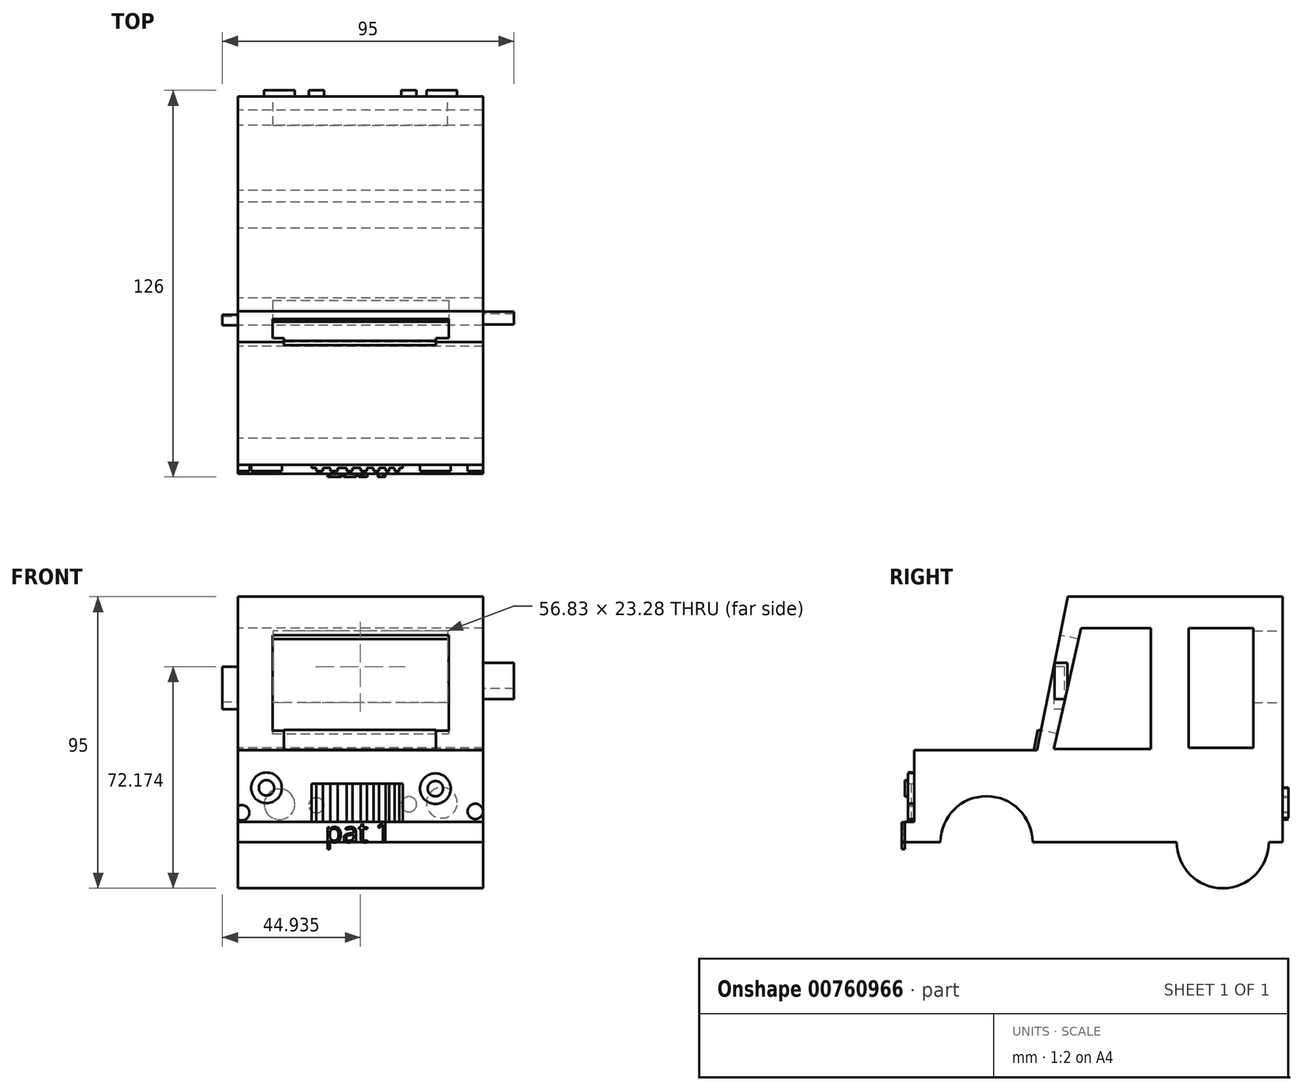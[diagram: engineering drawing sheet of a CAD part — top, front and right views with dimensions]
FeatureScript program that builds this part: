
annotation { "Feature Type Name" : "Feature", "Feature Type Description" : "" }
export const myFeature = defineFeature(function(context is Context, id is Id, definition is map)
    precondition{}
    {
        {
            var Q0;
            Q0=qCreatedBy(makeId("Right.planeOp"),FACE);
            var sketch = newSketch(context, id + "F0", { "sketchPlane" : qUnion([Q0])});
            skLineSegment(sketch, "E0", {"start": v(-60.4, -27.4) * mm, "end": v(59.6, -27.4) * mm});
            skLineSegment(sketch, "E1", {"start": v(59.6, -27.4) * mm, "end": v(59.6, 52.6) * mm});
            skLineSegment(sketch, "E2", {"start": v(59.6, 52.6) * mm, "end": v(-10.4, 52.6) * mm});
            skLineSegment(sketch, "E3", {"start": v(-10.4, 52.6) * mm, "end": v(-20.4, 2.6) * mm});
            skLineSegment(sketch, "E4", {"start": v(-20.4, 2.6) * mm, "end": v(-60.4, 2.6) * mm});
            skLineSegment(sketch, "E5", {"start": v(-60.4, 2.6) * mm, "end": v(-60.4, -27.4) * mm});
            skCircle(sketch, "E6", {"center": v(-36.83, -27.4) * mm, "radius": 15 * mm});
            skCircle(sketch, "E7", {"center": v(40.14, -27.4) * mm, "radius": 15 * mm});
            skSolve(sketch);
        }
        {
            var Q0;
            {var subQ0=sQuery(id+"F0.wireOp",EDGE,"E1");Q0=makeQuery(id+"F0.imprint","IMPRINT",FACE,{"disambiguationData":[TD([[makeQuery(id+"F0.imprint","IMPRINT",EDGE,{"derivedFrom":subQ0}),1.0]])]});}
            var Q1;
            {var subQ0=sQuery(id+"F0.wireOp",EDGE,"E6");var subQ1=sQuery(id+"F0.wireOp",EDGE,"E0");var subQ2=makeQuery(id+"F0.imprint","INTERSECT",VERTEX,{"disambiguationData":[OD(0.0)],"derivedFrom":[subQ1,subQ0]});Q1=makeQuery(id+"F0.imprint","IMPRINT",FACE,{"disambiguationData":[TD([[makeQuery(id+"F0.imprint","IMPRINT",EDGE,{"disambiguationData":[TD([[subQ2,-1.0]])],"derivedFrom":subQ1}),-1.0]])]});}
            var Q2;
            {var subQ0=sQuery(id+"F0.wireOp",EDGE,"E6");var subQ1=sQuery(id+"F0.wireOp",EDGE,"E0");var subQ2=makeQuery(id+"F0.imprint","INTERSECT",VERTEX,{"disambiguationData":[OD(0.0)],"derivedFrom":[subQ1,subQ0]});Q2=makeQuery(id+"F0.imprint","IMPRINT",FACE,{"disambiguationData":[TD([[makeQuery(id+"F0.imprint","IMPRINT",EDGE,{"disambiguationData":[TD([[subQ2,-1.0]])],"derivedFrom":subQ1}),1.0]])]});}
            var Q3;
            {var subQ0=sQuery(id+"F0.wireOp",EDGE,"E7");var subQ1=sQuery(id+"F0.wireOp",EDGE,"E0");var subQ2=makeQuery(id+"F0.imprint","INTERSECT",VERTEX,{"disambiguationData":[OD(0.0)],"derivedFrom":[subQ1,subQ0]});Q3=makeQuery(id+"F0.imprint","IMPRINT",FACE,{"disambiguationData":[TD([[makeQuery(id+"F0.imprint","IMPRINT",EDGE,{"disambiguationData":[TD([[subQ2,-1.0]])],"derivedFrom":subQ1}),-1.0]])]});}
            var Q4;
            {var subQ0=sQuery(id+"F0.wireOp",EDGE,"E7");var subQ1=sQuery(id+"F0.wireOp",EDGE,"E0");var subQ2=makeQuery(id+"F0.imprint","INTERSECT",VERTEX,{"disambiguationData":[OD(0.0)],"derivedFrom":[subQ1,subQ0]});Q4=makeQuery(id+"F0.imprint","IMPRINT",FACE,{"disambiguationData":[TD([[makeQuery(id+"F0.imprint","IMPRINT",EDGE,{"disambiguationData":[TD([[subQ2,-1.0]])],"derivedFrom":subQ1}),1.0]])]});}
            extrude(context, id + "F1", {"entities" : qUnion([Q0, Q1, Q2, Q3, Q4]), "depth" : 80 * mm, "offsetDistance" : 25 * mm});
        }
        {
            var Q0;
            Q0=makeQuery(id+"F1.opExtrude","SWEPT_FACE",FACE,{"disambiguationData":[OSD([sQuery(id+"F0.wireOp",EDGE,"E5")])]});
            var sketch = newSketch(context, id + "F2", { "sketchPlane" : qUnion([Q0])});
            skCircle(sketch, "E8", {"center": v(9.38, -9.68) * mm, "radius": 5 * mm});
            skCircle(sketch, "E9", {"center": v(64.4, -9.94) * mm, "radius": 5 * mm});
            skSolve(sketch);
        }
        {
            var Q0;
            Q0=makeQuery(id+"F2.imprint","IMPRINT",FACE,{"disambiguationData":[TD([[makeQuery(id+"F2.imprint","IMPRINT",EDGE,{"derivedFrom":sQuery(id+"F2.wireOp",EDGE,"E8")}),1.0]])]});
            var Q1;
            Q1=makeQuery(id+"F2.imprint","IMPRINT",FACE,{"disambiguationData":[TD([[makeQuery(id+"F2.imprint","IMPRINT",EDGE,{"derivedFrom":sQuery(id+"F2.wireOp",EDGE,"E9")}),1.0]])]});
            extrude(context, id + "F3", {"entities" : qUnion([Q0, Q1]), "operationType" : NewBodyOperationType.ADD, "depth" : 2 * mm, "offsetDistance" : 25 * mm});
        }
        {
            var Q0;
            Q0=makeQuery(id+"F1.opExtrude","SWEPT_FACE",FACE,{"disambiguationData":[OSD([sQuery(id+"F0.wireOp",EDGE,"E3")])]});
            var sketch = newSketch(context, id + "F4", { "sketchPlane" : qUnion([Q0])});
            skLineSegment(sketch, "E10.bottom", {"start": v(11.33, 36.75) * mm, "end": v(68.74, 36.75) * mm});
            skLineSegment(sketch, "E10.top", {"start": v(11.33, 5.1) * mm, "end": v(68.74, 5.1) * mm});
            skLineSegment(sketch, "E10.left", {"start": v(11.33, 36.75) * mm, "end": v(11.33, 5.1) * mm});
            skLineSegment(sketch, "E10.right", {"start": v(68.74, 36.75) * mm, "end": v(68.74, 5.1) * mm});
            skSolve(sketch);
        }
        {
            var Q0;
            Q0=makeQuery(id+"F4.imprint","IMPRINT",FACE,{"disambiguationData":[TD([[makeQuery(id+"F4.imprint","IMPRINT",EDGE,{"derivedFrom":sQuery(id+"F4.wireOp",EDGE,"E10.bottom")}),-1.0]])]});
            extrude(context, id + "F5", {"entities" : qUnion([Q0]), "operationType" : NewBodyOperationType.REMOVE, "oppositeDirection" : true, "depth" : 25 * mm, "offsetDistance" : 25 * mm});
        }
        {
            var Q0;
            Q0=makeQuery(id+"F1.opExtrude","SWEPT_FACE",FACE,{"disambiguationData":[OSD([sQuery(id+"F0.wireOp",EDGE,"E1")])]});
            var sketch = newSketch(context, id + "F6", { "sketchPlane" : qUnion([Q0])});
            skLineSegment(sketch, "E11.bottom", {"start": v(-68.35, 41.41) * mm, "end": v(-11.52, 41.41) * mm});
            skLineSegment(sketch, "E11.top", {"start": v(-68.35, 18.14) * mm, "end": v(-11.52, 18.14) * mm});
            skLineSegment(sketch, "E11.left", {"start": v(-68.35, 41.41) * mm, "end": v(-68.35, 18.14) * mm});
            skLineSegment(sketch, "E11.right", {"start": v(-11.52, 41.41) * mm, "end": v(-11.52, 18.14) * mm});
            skSolve(sketch);
        }
        {
            var Q0;
            Q0=makeQuery(id+"F6.imprint","IMPRINT",FACE,{"disambiguationData":[TD([[makeQuery(id+"F6.imprint","IMPRINT",EDGE,{"derivedFrom":sQuery(id+"F6.wireOp",EDGE,"E11.bottom")}),1.0]])]});
            var sketch = newSketch(context, id + "F7", { "sketchPlane" : qUnion([Q0])});
            skCircle(sketch, "E12", {"center": v(-66.49, -14.54) * mm, "radius": 5 * mm});
            skCircle(sketch, "E13", {"center": v(-13.63, -15.03) * mm, "radius": 5 * mm});
            skCircle(sketch, "E14", {"center": v(-55.79, -15.03) * mm, "radius": 2.5 * mm});
            skCircle(sketch, "E15", {"center": v(-25.65, -15.36) * mm, "radius": 2.5 * mm});
            skSolve(sketch);
        }
        {
            var Q0;
            Q0=makeQuery(id+"F6.imprint","IMPRINT",FACE,{"disambiguationData":[TD([[makeQuery(id+"F6.imprint","IMPRINT",EDGE,{"derivedFrom":sQuery(id+"F6.wireOp",EDGE,"E11.bottom")}),-1.0]])]});
            extrude(context, id + "F8", {"entities" : qUnion([Q0]), "operationType" : NewBodyOperationType.REMOVE, "oppositeDirection" : true, "depth" : 25 * mm, "offsetDistance" : 25 * mm});
        }
        {
            var Q0;
            Q0=makeQuery(id+"F7.imprint","IMPRINT",FACE,{"disambiguationData":[TD([[makeQuery(id+"F7.imprint","IMPRINT",EDGE,{"derivedFrom":sQuery(id+"F7.wireOp",EDGE,"E12")}),1.0]])]});
            var Q1;
            Q1=makeQuery(id+"F7.imprint","IMPRINT",FACE,{"disambiguationData":[TD([[makeQuery(id+"F7.imprint","IMPRINT",EDGE,{"derivedFrom":sQuery(id+"F7.wireOp",EDGE,"E14")}),1.0]])]});
            var Q2;
            Q2=makeQuery(id+"F7.imprint","IMPRINT",FACE,{"disambiguationData":[TD([[makeQuery(id+"F7.imprint","IMPRINT",EDGE,{"derivedFrom":sQuery(id+"F7.wireOp",EDGE,"E13")}),1.0]])]});
            var Q3;
            Q3=makeQuery(id+"F7.imprint","IMPRINT",FACE,{"disambiguationData":[TD([[makeQuery(id+"F7.imprint","IMPRINT",EDGE,{"derivedFrom":sQuery(id+"F7.wireOp",EDGE,"E15")}),1.0]])]});
            extrude(context, id + "F9", {"entities" : qUnion([Q0, Q1, Q2, Q3]), "operationType" : NewBodyOperationType.ADD, "depth" : 2 * mm, "offsetDistance" : 25 * mm});
        }
        {
            var Q0;
            Q0=makeQuery(id+"F1.opExtrude","CAP_FACE",FACE,{"disambiguationData":[OSD([sQuery(id+"F0.wireOp",EDGE,"E0"),sQuery(id+"F0.wireOp",EDGE,"E1"),sQuery(id+"F0.wireOp",EDGE,"E2"),sQuery(id+"F0.wireOp",EDGE,"E3"),sQuery(id+"F0.wireOp",EDGE,"E4"),sQuery(id+"F0.wireOp",EDGE,"E5"),sQuery(id+"F0.wireOp",EDGE,"E6"),sQuery(id+"F0.wireOp",EDGE,"E7")])],"isStart":true});
            var sketch = newSketch(context, id + "F10", { "sketchPlane" : qUnion([Q0])});
            skLineSegment(sketch, "E16", {"start": v(-16.68, 42.4) * mm, "end": v(6.01, 42.4) * mm});
            skLineSegment(sketch, "E17", {"start": v(6.01, 42.4) * mm, "end": v(14.94, 2.99) * mm});
            skLineSegment(sketch, "E18", {"start": v(14.94, 2.99) * mm, "end": v(-16.68, 2.99) * mm});
            skLineSegment(sketch, "E19", {"start": v(-16.68, 2.99) * mm, "end": v(-16.68, 42.4) * mm});
            skSolve(sketch);
        }
        {
            var Q0;
            Q0=makeQuery(id+"F10.imprint","IMPRINT",FACE,{"disambiguationData":[TD([[makeQuery(id+"F10.imprint","IMPRINT",EDGE,{"derivedFrom":sQuery(id+"F10.wireOp",EDGE,"E16")}),1.0]])]});
            var sketch = newSketch(context, id + "F11", { "sketchPlane" : qUnion([Q0])});
            skLineSegment(sketch, "E20.bottom", {"start": v(-50.14, 42.38) * mm, "end": v(-29, 42.38) * mm});
            skLineSegment(sketch, "E20.top", {"start": v(-50.14, 3.4) * mm, "end": v(-29, 3.4) * mm});
            skLineSegment(sketch, "E20.left", {"start": v(-50.14, 42.38) * mm, "end": v(-50.14, 3.4) * mm});
            skLineSegment(sketch, "E20.right", {"start": v(-29, 42.38) * mm, "end": v(-29, 3.4) * mm});
            skSolve(sketch);
        }
        {
            var Q0;
            Q0=makeQuery(id+"F11.imprint","IMPRINT",FACE,{"disambiguationData":[TD([[makeQuery(id+"F11.imprint","IMPRINT",EDGE,{"derivedFrom":sQuery(id+"F11.wireOp",EDGE,"E20.bottom")}),-1.0]])]});
            var Q1;
            Q1=makeQuery(id+"F11.imprint","IMPRINT",FACE,{"disambiguationData":[TD([[makeQuery(id+"F11.imprint","IMPRINT",EDGE,{"derivedFrom":makeQuery(id+"F10.imprint","IMPRINT",EDGE,{"derivedFrom":sQuery(id+"F10.wireOp",EDGE,"E16")})}),-1.0]])]});
            extrude(context, id + "F12", {"entities" : qUnion([Q0, Q1]), "operationType" : NewBodyOperationType.REMOVE, "oppositeDirection" : true, "depth" : 100 * mm, "offsetDistance" : 25 * mm});
        }
        {
            var Q0;
            Q0=makeQuery(id+"F1.opExtrude","SWEPT_FACE",FACE,{"disambiguationData":[OSD([sQuery(id+"F0.wireOp",EDGE,"E3")])]});
            var sketch = newSketch(context, id + "F13", { "sketchPlane" : qUnion([Q0])});
            skLineSegment(sketch, "E21.bottom", {"start": v(15, 5.1) * mm, "end": v(64.59, 5.1) * mm});
            skLineSegment(sketch, "E21.top", {"start": v(15, -1.45) * mm, "end": v(64.59, -1.45) * mm});
            skLineSegment(sketch, "E21.left", {"start": v(15, 5.1) * mm, "end": v(15, -1.45) * mm});
            skLineSegment(sketch, "E21.right", {"start": v(64.59, 5.1) * mm, "end": v(64.59, -1.45) * mm});
            skSolve(sketch);
        }
        {
            var Q0;
            Q0=makeQuery(id+"F13.imprint","IMPRINT",FACE,{"disambiguationData":[TD([[makeQuery(id+"F13.imprint","IMPRINT",EDGE,{"derivedFrom":sQuery(id+"F13.wireOp",EDGE,"E21.bottom")}),-1.0]])]});
            extrude(context, id + "F14", {"entities" : qUnion([Q0]), "operationType" : NewBodyOperationType.ADD, "depth" : 1 * mm, "offsetDistance" : 25 * mm});
        }
        {
            var Q0;
            Q0=makeQuery(id+"F1.opExtrude","SWEPT_FACE",FACE,{"disambiguationData":[OSD([sQuery(id+"F0.wireOp",EDGE,"E5")])]});
            var sketch = newSketch(context, id + "F15", { "sketchPlane" : qUnion([Q0])});
            skLineSegment(sketch, "E22.bottom", {"start": v(0, -20.79) * mm, "end": v(80, -20.79) * mm});
            skLineSegment(sketch, "E22.top", {"start": v(0, -27.4) * mm, "end": v(80, -27.4) * mm});
            skLineSegment(sketch, "E22.left", {"start": v(0, -20.79) * mm, "end": v(0, -27.4) * mm});
            skLineSegment(sketch, "E22.right", {"start": v(80, -20.79) * mm, "end": v(80, -27.4) * mm});
            skSolve(sketch);
        }
        {
            var Q0;
            Q0=makeQuery(id+"F15.imprint","IMPRINT",FACE,{"disambiguationData":[TD([[makeQuery(id+"F15.imprint","IMPRINT",EDGE,{"derivedFrom":sQuery(id+"F15.wireOp",EDGE,"E22.bottom")}),-1.0]])]});
            extrude(context, id + "F16", {"entities" : qUnion([Q0]), "operationType" : NewBodyOperationType.ADD, "depth" : 3 * mm, "offsetDistance" : 25 * mm});
        }
        {
            var Q0;
            Q0=makeQuery(id+"F1.opExtrude","SWEPT_FACE",FACE,{"disambiguationData":[OSD([sQuery(id+"F0.wireOp",EDGE,"E5")])]});
            var sketch = newSketch(context, id + "F17", { "sketchPlane" : qUnion([Q0])});
            skCircle(sketch, "E23", {"center": v(1.31, -17.78) * mm, "radius": 2.5 * mm});
            skCircle(sketch, "E24", {"center": v(77.4, -17.35) * mm, "radius": 2.5 * mm});
            skSolve(sketch);
        }
        {
            var Q0;
            {var subQ0=sQuery(id+"F17.wireOp",EDGE,"E23");var subQ1=makeQuery(id+"F1.opExtrude","CAP_EDGE",EDGE,{"disambiguationData":[OSD([sQuery(id+"F0.wireOp",EDGE,"E5")])],"isStart":true});var subQ2=makeQuery(id+"F17.imprint","INTERSECT",VERTEX,{"disambiguationData":[OD(0.0)],"derivedFrom":[subQ1,subQ0]});Q0=makeQuery(id+"F17.imprint","IMPRINT",FACE,{"disambiguationData":[TD([[makeQuery(id+"F17.imprint","IMPRINT",EDGE,{"disambiguationData":[TD([[subQ2,1.0]])],"derivedFrom":subQ0}),1.0]])]});}
            var Q1;
            Q1=makeQuery(id+"F17.imprint","IMPRINT",FACE,{"disambiguationData":[TD([[makeQuery(id+"F17.imprint","IMPRINT",EDGE,{"derivedFrom":sQuery(id+"F17.wireOp",EDGE,"E24")}),1.0]])]});
            extrude(context, id + "F18", {"entities" : qUnion([Q0, Q1]), "operationType" : NewBodyOperationType.ADD, "depth" : 2 * mm, "offsetDistance" : 25 * mm});
        }
        {
            var Q0;
            Q0=makeQuery(id+"F1.opExtrude","SWEPT_FACE",FACE,{"disambiguationData":[OSD([sQuery(id+"F0.wireOp",EDGE,"E5")])]});
            var sketch = newSketch(context, id + "F19", { "sketchPlane" : qUnion([Q0])});
            skLineSegment(sketch, "E25.bottom", {"start": v(24.1, -8.3) * mm, "end": v(53.73, -8.3) * mm});
            skLineSegment(sketch, "E25.top", {"start": v(24.1, -20.79) * mm, "end": v(53.73, -20.79) * mm});
            skLineSegment(sketch, "E25.left", {"start": v(24.1, -8.3) * mm, "end": v(24.1, -20.79) * mm});
            skLineSegment(sketch, "E25.right", {"start": v(53.73, -8.3) * mm, "end": v(53.73, -20.79) * mm});
            skSolve(sketch);
        }
        {
            var Q0;
            Q0=makeQuery(id+"F19.imprint","IMPRINT",FACE,{"disambiguationData":[TD([[makeQuery(id+"F19.imprint","IMPRINT",EDGE,{"derivedFrom":sQuery(id+"F19.wireOp",EDGE,"E25.bottom")}),-1.0]])]});
            extrude(context, id + "F20", {"entities" : qUnion([Q0]), "operationType" : NewBodyOperationType.ADD, "depth" : 1 * mm, "offsetDistance" : 25 * mm});
        }
        {
            var Q0;
            Q0=makeQuery(id+"F20.opExtrude","CAP_FACE",FACE,{"disambiguationData":[OSD([sQuery(id+"F19.wireOp",EDGE,"E25.bottom"),sQuery(id+"F19.wireOp",EDGE,"E25.top"),sQuery(id+"F19.wireOp",EDGE,"E25.left"),sQuery(id+"F19.wireOp",EDGE,"E25.right")])],"isStart":false});
            var sketch = newSketch(context, id + "F21", { "sketchPlane" : qUnion([Q0])});
            skLineSegment(sketch, "E26.bottom", {"start": v(25.56, -8.3) * mm, "end": v(27.7, -8.3) * mm});
            skLineSegment(sketch, "E26.top", {"start": v(25.56, -20.79) * mm, "end": v(27.7, -20.79) * mm});
            skLineSegment(sketch, "E26.left", {"start": v(25.56, -8.3) * mm, "end": v(25.56, -20.79) * mm});
            skLineSegment(sketch, "E26.right", {"start": v(27.7, -8.3) * mm, "end": v(27.7, -20.79) * mm});
            skLineSegment(sketch, "E27.bottom", {"start": v(30.22, -8.3) * mm, "end": v(32.55, -8.3) * mm});
            skLineSegment(sketch, "E27.top", {"start": v(30.22, -20.79) * mm, "end": v(32.55, -20.79) * mm});
            skLineSegment(sketch, "E27.left", {"start": v(30.22, -8.3) * mm, "end": v(30.22, -20.79) * mm});
            skLineSegment(sketch, "E27.right", {"start": v(32.55, -8.3) * mm, "end": v(32.55, -20.79) * mm});
            skLineSegment(sketch, "E28.bottom", {"start": v(35.46, -8.3) * mm, "end": v(37.4, -8.3) * mm});
            skLineSegment(sketch, "E28.top", {"start": v(35.46, -20.79) * mm, "end": v(37.4, -20.79) * mm});
            skLineSegment(sketch, "E28.left", {"start": v(35.46, -8.3) * mm, "end": v(35.46, -20.79) * mm});
            skLineSegment(sketch, "E28.right", {"start": v(37.4, -8.3) * mm, "end": v(37.4, -20.79) * mm});
            skLineSegment(sketch, "E29.bottom", {"start": v(40.01, -8.3) * mm, "end": v(42.15, -8.3) * mm});
            skLineSegment(sketch, "E29.top", {"start": v(40.01, -20.79) * mm, "end": v(42.15, -20.79) * mm});
            skLineSegment(sketch, "E29.left", {"start": v(40.01, -8.3) * mm, "end": v(40.01, -20.79) * mm});
            skLineSegment(sketch, "E29.right", {"start": v(42.15, -8.3) * mm, "end": v(42.15, -20.79) * mm});
            skLineSegment(sketch, "E30.bottom", {"start": v(44.28, -8.3) * mm, "end": v(46.03, -8.3) * mm});
            skLineSegment(sketch, "E30.top", {"start": v(44.28, -20.79) * mm, "end": v(46.03, -20.79) * mm});
            skLineSegment(sketch, "E30.left", {"start": v(44.28, -8.3) * mm, "end": v(44.28, -20.79) * mm});
            skLineSegment(sketch, "E30.right", {"start": v(46.03, -8.3) * mm, "end": v(46.03, -20.79) * mm});
            skLineSegment(sketch, "E31.bottom", {"start": v(48.16, -8.3) * mm, "end": v(49.32, -8.3) * mm});
            skLineSegment(sketch, "E31.top", {"start": v(48.16, -20.79) * mm, "end": v(49.32, -20.79) * mm});
            skLineSegment(sketch, "E31.left", {"start": v(48.16, -8.3) * mm, "end": v(48.16, -20.79) * mm});
            skLineSegment(sketch, "E31.right", {"start": v(49.32, -8.3) * mm, "end": v(49.32, -20.79) * mm});
            skLineSegment(sketch, "E32.bottom", {"start": v(51.17, -8.3) * mm, "end": v(52.62, -8.3) * mm});
            skLineSegment(sketch, "E32.top", {"start": v(51.17, -20.79) * mm, "end": v(52.62, -20.79) * mm});
            skLineSegment(sketch, "E32.left", {"start": v(51.17, -8.3) * mm, "end": v(51.17, -20.79) * mm});
            skLineSegment(sketch, "E32.right", {"start": v(52.62, -8.3) * mm, "end": v(52.62, -20.79) * mm});
            skSolve(sketch);
        }
        {
            var Q0;
            Q0=makeQuery(id+"F21.imprint","IMPRINT",FACE,{"disambiguationData":[TD([[makeQuery(id+"F21.imprint","IMPRINT",EDGE,{"derivedFrom":sQuery(id+"F21.wireOp",EDGE,"E26.bottom")}),-1.0]])]});
            var Q1;
            Q1=makeQuery(id+"F21.imprint","IMPRINT",FACE,{"disambiguationData":[TD([[makeQuery(id+"F21.imprint","IMPRINT",EDGE,{"derivedFrom":sQuery(id+"F21.wireOp",EDGE,"E27.bottom")}),-1.0]])]});
            var Q2;
            Q2=makeQuery(id+"F21.imprint","IMPRINT",FACE,{"disambiguationData":[TD([[makeQuery(id+"F21.imprint","IMPRINT",EDGE,{"derivedFrom":sQuery(id+"F21.wireOp",EDGE,"E28.bottom")}),-1.0]])]});
            var Q3;
            Q3=makeQuery(id+"F21.imprint","IMPRINT",FACE,{"disambiguationData":[TD([[makeQuery(id+"F21.imprint","IMPRINT",EDGE,{"derivedFrom":sQuery(id+"F21.wireOp",EDGE,"E29.bottom")}),-1.0]])]});
            var Q4;
            Q4=makeQuery(id+"F21.imprint","IMPRINT",FACE,{"disambiguationData":[TD([[makeQuery(id+"F21.imprint","IMPRINT",EDGE,{"derivedFrom":sQuery(id+"F21.wireOp",EDGE,"E30.bottom")}),-1.0]])]});
            var Q5;
            Q5=makeQuery(id+"F21.imprint","IMPRINT",FACE,{"disambiguationData":[TD([[makeQuery(id+"F21.imprint","IMPRINT",EDGE,{"derivedFrom":sQuery(id+"F21.wireOp",EDGE,"E31.bottom")}),-1.0]])]});
            var Q6;
            Q6=makeQuery(id+"F21.imprint","IMPRINT",FACE,{"disambiguationData":[TD([[makeQuery(id+"F21.imprint","IMPRINT",EDGE,{"derivedFrom":sQuery(id+"F21.wireOp",EDGE,"E32.bottom")}),-1.0]])]});
            extrude(context, id + "F22", {"entities" : qUnion([Q0, Q1, Q2, Q3, Q4, Q5, Q6]), "operationType" : NewBodyOperationType.ADD, "depth" : 1 * mm, "offsetDistance" : 25 * mm});
        }
        {
            var Q0;
            Q0=makeQuery(id+"F16.opExtrude","CAP_FACE",FACE,{"disambiguationData":[OSD([sQuery(id+"F15.wireOp",EDGE,"E22.bottom"),sQuery(id+"F15.wireOp",EDGE,"E22.top"),sQuery(id+"F15.wireOp",EDGE,"E22.left"),sQuery(id+"F15.wireOp",EDGE,"E22.right")])],"isStart":false});
            var sketch = newSketch(context, id + "F23", { "sketchPlane" : qUnion([Q0])});
            skText(sketch, "E33", { "text": "pat 1", "fontName": "OpenSans-Regular.ttf"});
            const initialGuessF23  = {"E33": [0.0285, -0.0274, 1, 0, 0.00661]};
            skSetInitialGuess(sketch, initialGuessF23);
            skSolve(sketch);
        }
        {
            var Q0;
            Q0 = qSketchRegion(id + "F23", true);
            extrude(context, id + "F24", {"entities" : qUnion([Q0]), "operationType" : NewBodyOperationType.ADD, "depth" : 1 * mm, "offsetDistance" : 25 * mm});
        }
        {
            var Q0;
            Q0=makeQuery(id+"F3.opExtrude","CAP_FACE",FACE,{"disambiguationData":[OSD([sQuery(id+"F2.wireOp",EDGE,"E8")])],"isStart":false});
            var sketch = newSketch(context, id + "F25", { "sketchPlane" : qUnion([Q0])});
            skCircle(sketch, "E34", {"center": v(9.38, -9.68) * mm, "radius": 2.5 * mm});
            skSolve(sketch);
        }
        {
            var Q0;
            Q0=makeQuery(id+"F3.opExtrude","CAP_FACE",FACE,{"disambiguationData":[OSD([sQuery(id+"F2.wireOp",EDGE,"E9")])],"isStart":false});
            var sketch = newSketch(context, id + "F26", { "sketchPlane" : qUnion([Q0])});
            skCircle(sketch, "E35", {"center": v(64.4, -9.94) * mm, "radius": 2.5 * mm});
            skSolve(sketch);
        }
        {
            var Q0;
            Q0=makeQuery(id+"F26.imprint","IMPRINT",FACE,{"disambiguationData":[TD([[makeQuery(id+"F26.imprint","IMPRINT",EDGE,{"derivedFrom":sQuery(id+"F26.wireOp",EDGE,"E35")}),1.0]])]});
            var Q1;
            Q1=makeQuery(id+"F25.imprint","IMPRINT",FACE,{"disambiguationData":[TD([[makeQuery(id+"F25.imprint","IMPRINT",EDGE,{"derivedFrom":sQuery(id+"F25.wireOp",EDGE,"E34")}),1.0]])]});
            extrude(context, id + "F27", {"entities" : qUnion([Q0, Q1]), "operationType" : NewBodyOperationType.ADD, "depth" : 1 * mm, "offsetDistance" : 25 * mm});
        }
        {
            var Q0;
            Q0=makeQuery(id+"F10.imprint","IMPRINT",FACE,{"disambiguationData":[TD([[makeQuery(id+"F10.imprint","IMPRINT",EDGE,{"derivedFrom":sQuery(id+"F10.wireOp",EDGE,"E16")}),1.0]])]});
            var sketch = newSketch(context, id + "F28", { "sketchPlane" : qUnion([Q0])});
            skLineSegment(sketch, "E36.bottom", {"start": v(11.46, 29.77) * mm, "end": v(14.95, 29.77) * mm});
            skLineSegment(sketch, "E36.top", {"start": v(11.46, 16) * mm, "end": v(14.95, 16) * mm});
            skLineSegment(sketch, "E36.left", {"start": v(11.46, 29.77) * mm, "end": v(11.46, 16) * mm});
            skLineSegment(sketch, "E36.right", {"start": v(14.95, 29.77) * mm, "end": v(14.95, 16) * mm});
            skSolve(sketch);
        }
        {
            var Q0;
            {var subQ1=sQuery(id+"F28.wireOp",EDGE,"E36.bottom");Q0=makeQuery(id+"F28.imprint","IMPRINT",FACE,{"disambiguationData":[TD([[makeQuery(id+"F28.imprint","IMPRINT",EDGE,{"derivedFrom":subQ1}),-1.0]])]});}
            extrude(context, id + "F29", {"entities" : qUnion([Q0]), "operationType" : NewBodyOperationType.ADD, "depth" : 5 * mm, "offsetDistance" : 25 * mm});
        }
        {
            var Q0;
            Q0=makeQuery(id+"F16.boolean.opBoolean","MERGE",FACE,{"derivedFrom":[makeQuery(id+"F1.opExtrude","CAP_FACE",FACE,{"disambiguationData":[OSD([sQuery(id+"F0.wireOp",EDGE,"E0"),sQuery(id+"F0.wireOp",EDGE,"E1"),sQuery(id+"F0.wireOp",EDGE,"E2"),sQuery(id+"F0.wireOp",EDGE,"E3"),sQuery(id+"F0.wireOp",EDGE,"E4"),sQuery(id+"F0.wireOp",EDGE,"E5"),sQuery(id+"F0.wireOp",EDGE,"E6"),sQuery(id+"F0.wireOp",EDGE,"E7")])],"isStart":false}),makeQuery(id+"F16.opExtrude","SWEPT_FACE",FACE,{"disambiguationData":[OSD([sQuery(id+"F15.wireOp",EDGE,"E22.right")])]})]});
            var sketch = newSketch(context, id + "F30", { "sketchPlane" : qUnion([Q0])});
            skPoint(sketch, "E37.oppositeSnap0", {"position": v(-10.47, 22.7) * mm});
            skLineSegment(sketch, "E37.bottom", {"start": v(-14.7, 31.1) * mm, "end": v(-10.47, 31.1) * mm});
            skLineSegment(sketch, "E37.top", {"start": v(-14.7, 19.2) * mm, "end": v(-10.47, 19.2) * mm});
            skLineSegment(sketch, "E37.left", {"start": v(-14.7, 31.1) * mm, "end": v(-14.7, 19.2) * mm});
            skLineSegment(sketch, "E37.right", {"start": v(-10.47, 31.1) * mm, "end": v(-10.47, 19.2) * mm});
            skSolve(sketch);
        }
        {
            var Q0;
            {var subQ1=sQuery(id+"F30.wireOp",EDGE,"E37.bottom");Q0=makeQuery(id+"F30.imprint","IMPRINT",FACE,{"disambiguationData":[TD([[makeQuery(id+"F30.imprint","IMPRINT",EDGE,{"derivedFrom":subQ1}),-1.0]])]});}
            extrude(context, id + "F31", {"entities" : qUnion([Q0]), "operationType" : NewBodyOperationType.ADD, "depth" : 10 * mm, "offsetDistance" : 25 * mm});
        }
    });
